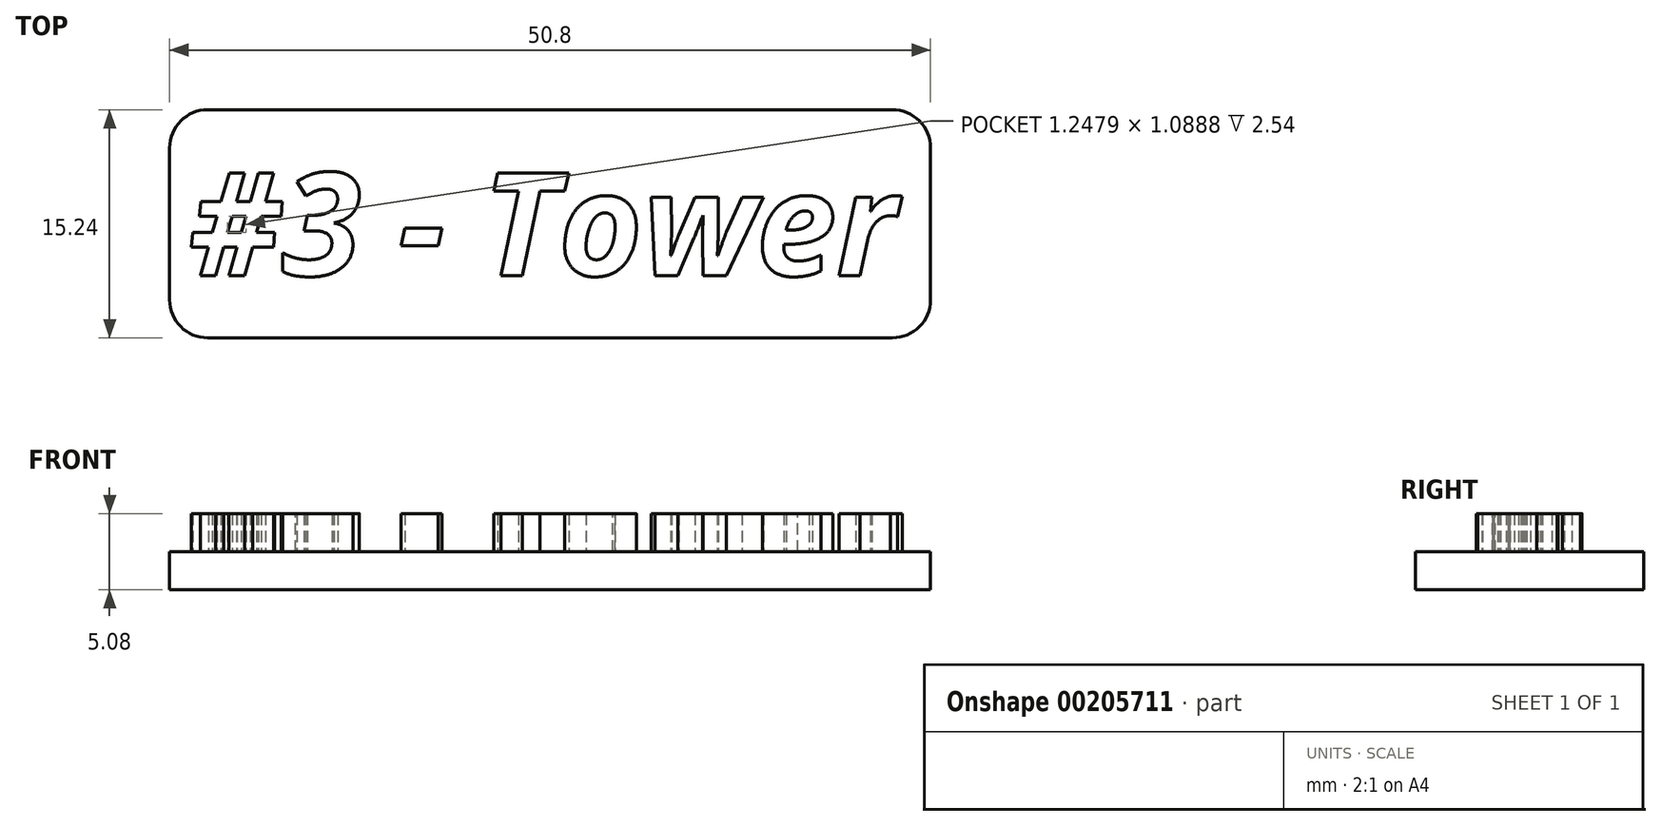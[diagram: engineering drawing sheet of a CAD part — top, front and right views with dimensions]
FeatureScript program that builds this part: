
annotation { "Feature Type Name" : "Feature", "Feature Type Description" : "" }
export const myFeature = defineFeature(function(context is Context, id is Id, definition is map)
    precondition{}
    {
        {
            var Q0;
            Q0=qCreatedBy(makeId("Top.planeOp"),FACE);
            var sketch = newSketch(context, id + "F0", { "sketchPlane" : qUnion([Q0])});
            skLineSegment(sketch, "E0.bottom", {"start": v(-25.4, 7.62) * mm, "end": v(25.4, 7.62) * mm});
            skLineSegment(sketch, "E0.top", {"start": v(-25.4, -7.62) * mm, "end": v(25.4, -7.62) * mm});
            skLineSegment(sketch, "E0.left", {"start": v(-25.4, 7.62) * mm, "end": v(-25.4, -7.62) * mm});
            skLineSegment(sketch, "E0.right", {"start": v(25.4, 7.62) * mm, "end": v(25.4, -7.62) * mm});
            skPoint(sketch, "E0.middle", {"position": v(0, 0) * mm});
            skSolve(sketch);
        }
        {
            var Q0;
            Q0 = qSketchRegion(id + "F0", true);
            extrude(context, id + "F1", {"entities" : qUnion([Q0]), "depth" : 2.54 * mm});
        }
        {
            var Q0;
            Q0=makeQuery(id+"F1.opExtrude","CAP_FACE",FACE,{"disambiguationData":[OSD([sQuery(id+"F0.wireOp",EDGE,"E0.bottom"),sQuery(id+"F0.wireOp",EDGE,"E0.top"),sQuery(id+"F0.wireOp",EDGE,"E0.left"),sQuery(id+"F0.wireOp",EDGE,"E0.right")])],"isStart":false});
            var sketch = newSketch(context, id + "F2", { "sketchPlane" : qUnion([Q0])});
            skText(sketch, "E1", { "text": "#3 - Tower", "fontName": "OpenSans-BoldItalic.ttf"});
            skPoint(sketch, "E2", {"position": v(-24.13, 0) * mm});
            const initialGuessF2  = {"E1": [-0.02413, -0.00346, 1, 0, 0.00692]};
            skSetInitialGuess(sketch, initialGuessF2);
            skSolve(sketch);
        }
        {
            var Q0;
            Q0 = qSketchRegion(id + "F2", true);
            extrude(context, id + "F3", {"entities" : qUnion([Q0]), "operationType" : NewBodyOperationType.ADD, "depth" : 2.54 * mm});
        }
        {
            var Q0;
            Q0=makeQuery(id+"F1.opExtrude","SWEPT_EDGE",EDGE,{"disambiguationData":[OSD([sQuery(id+"F0.wireOp",EDGE,"E0.bottom"),sQuery(id+"F0.wireOp",EDGE,"E0.left")])]});
            var Q1;
            Q1=makeQuery(id+"F1.opExtrude","SWEPT_EDGE",EDGE,{"disambiguationData":[OSD([sQuery(id+"F0.wireOp",EDGE,"E0.top"),sQuery(id+"F0.wireOp",EDGE,"E0.left")])]});
            var Q2;
            Q2=makeQuery(id+"F1.opExtrude","SWEPT_EDGE",EDGE,{"disambiguationData":[OSD([sQuery(id+"F0.wireOp",EDGE,"E0.top"),sQuery(id+"F0.wireOp",EDGE,"E0.right")])]});
            var Q3;
            Q3=makeQuery(id+"F1.opExtrude","SWEPT_EDGE",EDGE,{"disambiguationData":[OSD([sQuery(id+"F0.wireOp",EDGE,"E0.bottom"),sQuery(id+"F0.wireOp",EDGE,"E0.right")])]});
            fillet(context, id + "F4", {"entities" : qUnion([Q0, Q1, Q2, Q3]), "radius" : 2.54 * mm, "tangentPropagation" : true, "allowEdgeOverflow" : false});
        }
    });
